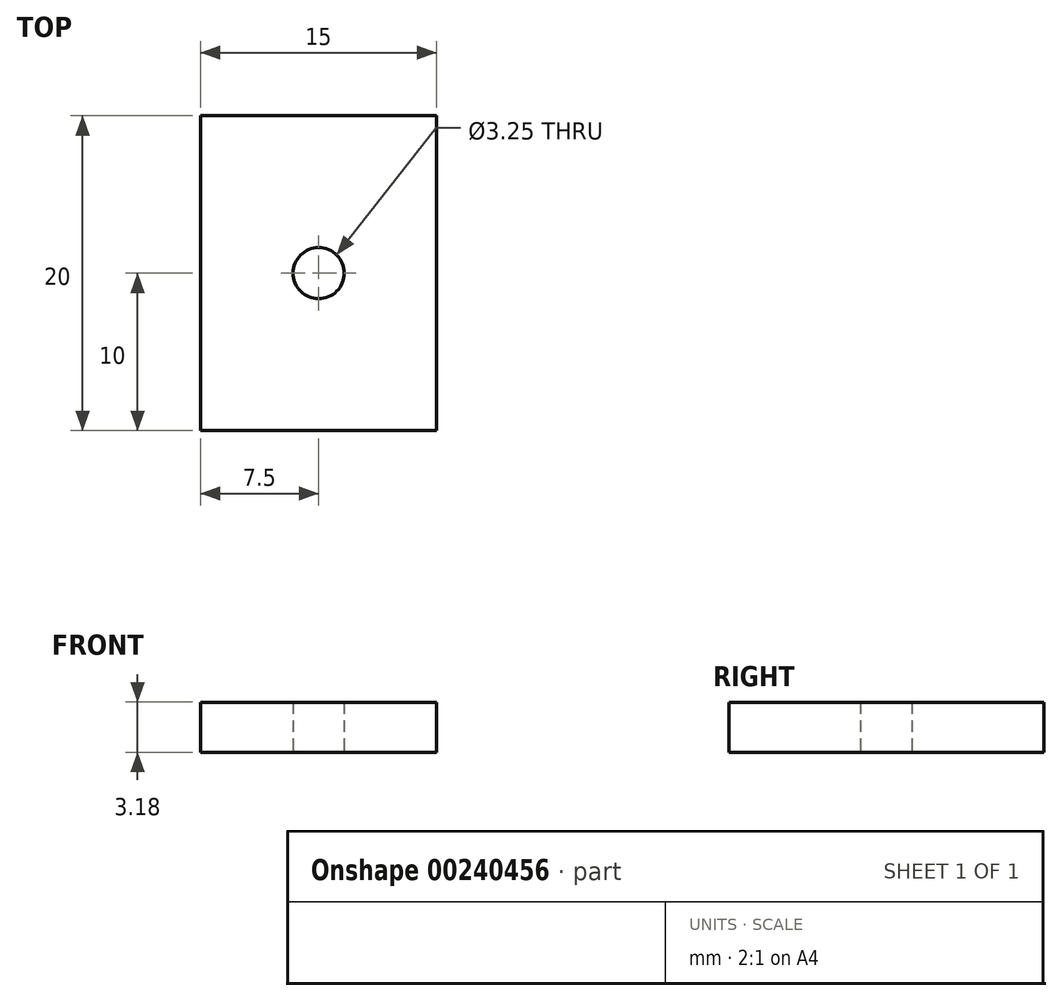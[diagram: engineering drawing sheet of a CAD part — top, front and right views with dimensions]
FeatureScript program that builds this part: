
annotation { "Feature Type Name" : "Feature", "Feature Type Description" : "" }
export const myFeature = defineFeature(function(context is Context, id is Id, definition is map)
    precondition{}
    {
        {
            var Q0;
            Q0=qCreatedBy(makeId("Top.planeOp"),FACE);
            var sketch = newSketch(context, id + "F0", { "sketchPlane" : qUnion([Q0])});
            skLineSegment(sketch, "E0.bottom", {"start": v(0, 0) * mm, "end": v(15, 0) * mm});
            skLineSegment(sketch, "E0.top", {"start": v(0, 20) * mm, "end": v(15, 20) * mm});
            skLineSegment(sketch, "E0.left", {"start": v(0, 0) * mm, "end": v(0, 20) * mm});
            skLineSegment(sketch, "E0.right", {"start": v(15, 0) * mm, "end": v(15, 20) * mm});
            skCircle(sketch, "E1", {"center": v(7.5, 10) * mm, "radius": 1.63 * mm});
            skPoint(sketch, "E1.centerSnap0", {"position": v(7.5, 0) * mm});
            skPoint(sketch, "E1.centerSnap1", {"position": v(0, 10) * mm});
            skSolve(sketch);
        }
        {
            var Q0;
            Q0 = qSketchRegion(id + "F0", true);
            extrude(context, id + "F1", {"entities" : qUnion([Q0]), "depth" : 3.17 * mm});
        }
    });
